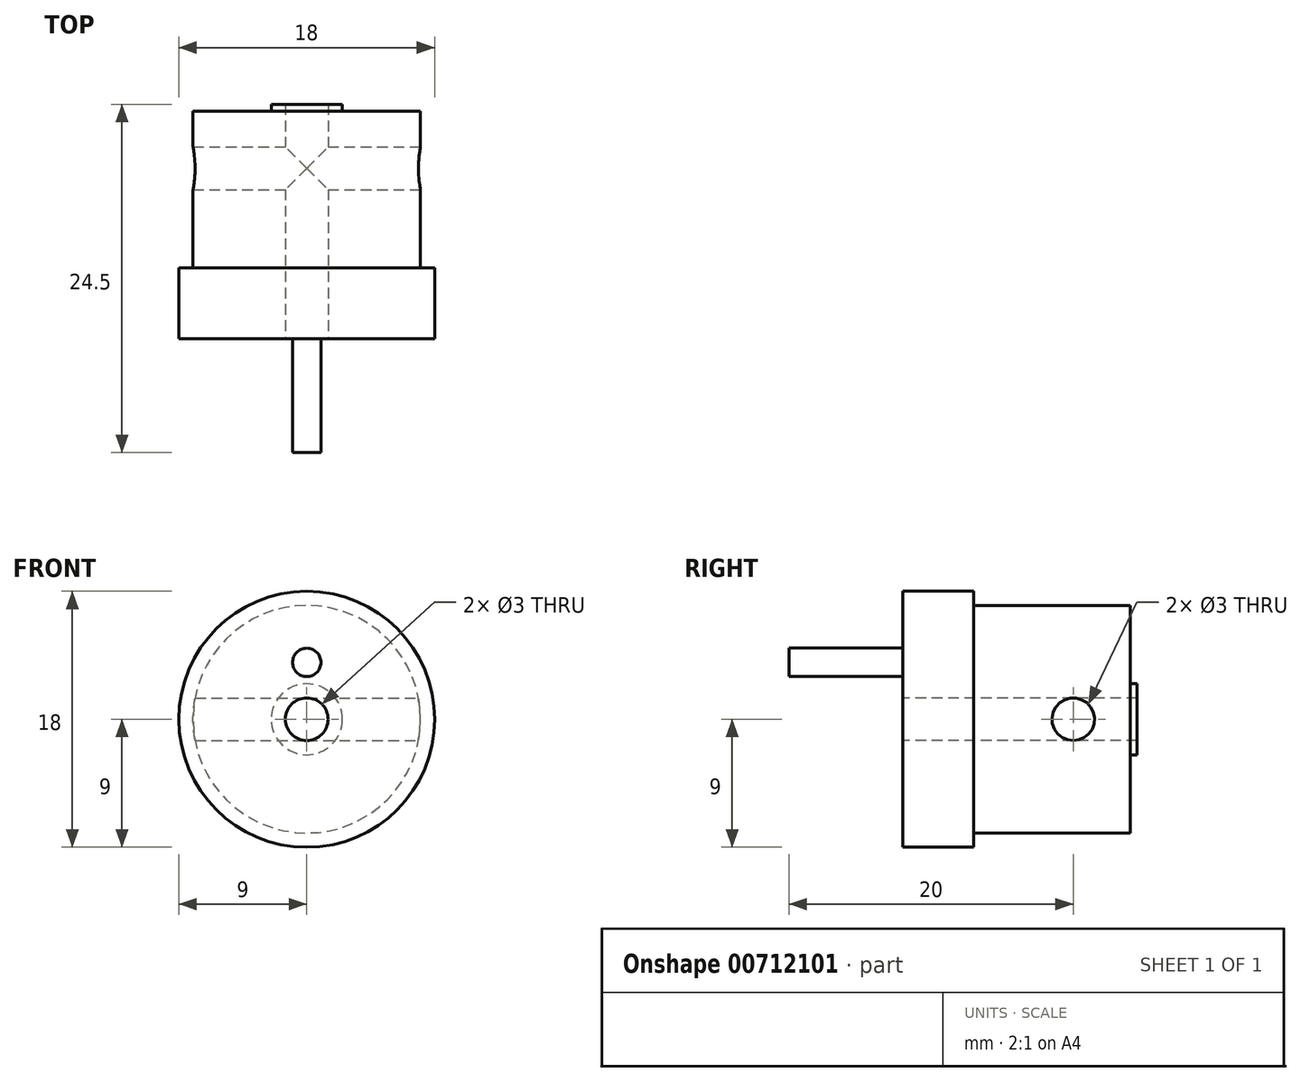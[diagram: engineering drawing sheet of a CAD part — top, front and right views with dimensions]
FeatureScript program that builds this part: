
annotation { "Feature Type Name" : "Feature", "Feature Type Description" : "" }
export const myFeature = defineFeature(function(context is Context, id is Id, definition is map)
    precondition{}
    {
        {
            var Q0;
            Q0=qCreatedBy(makeId("Front.planeOp"),FACE);
            var sketch = newSketch(context, id + "F0", { "sketchPlane" : qUnion([Q0])});
            skCircle(sketch, "E0", {"center": v(0, 0) * mm, "radius": 9 * mm});
            skCircle(sketch, "E1", {"center": v(0, 0) * mm, "radius": 8 * mm});
            skSolve(sketch);
        }
        {
            var Q0;
            Q0=makeQuery(id+"F0.imprint","IMPRINT",FACE,{"disambiguationData":[TD([[makeQuery(id+"F0.imprint","IMPRINT",EDGE,{"derivedFrom":sQuery(id+"F0.wireOp",EDGE,"E0")}),1.0]])]});
            var Q1;
            Q1=makeQuery(id+"F0.imprint","IMPRINT",FACE,{"disambiguationData":[TD([[makeQuery(id+"F0.imprint","IMPRINT",EDGE,{"derivedFrom":sQuery(id+"F0.wireOp",EDGE,"E1")}),1.0]])]});
            extrude(context, id + "F1", {"entities" : qUnion([Q0, Q1]), "depth" : 5 * mm, "offsetDistance" : 25 * mm});
        }
        {
            var Q0;
            Q0=makeQuery(id+"F0.imprint","IMPRINT",FACE,{"disambiguationData":[TD([[makeQuery(id+"F0.imprint","IMPRINT",EDGE,{"derivedFrom":sQuery(id+"F0.wireOp",EDGE,"E1")}),1.0]])]});
            extrude(context, id + "F2", {"entities" : qUnion([Q0]), "operationType" : NewBodyOperationType.ADD, "oppositeDirection" : true, "depth" : 11 * mm, "offsetDistance" : 25 * mm});
        }
        {
            var Q0;
            Q0=makeQuery(id+"F2.opExtrude","CAP_FACE",FACE,{"disambiguationData":[OSD([sQuery(id+"F0.wireOp",EDGE,"E1")])],"isStart":false});
            var sketch = newSketch(context, id + "F3", { "sketchPlane" : qUnion([Q0])});
            skCircle(sketch, "E2", {"center": v(0, 0) * mm, "radius": 2.5 * mm});
            skSolve(sketch);
        }
        {
            var Q0;
            Q0=makeQuery(id+"F3.imprint","IMPRINT",FACE,{"disambiguationData":[TD([[makeQuery(id+"F3.imprint","IMPRINT",EDGE,{"derivedFrom":sQuery(id+"F3.wireOp",EDGE,"E2")}),1.0]])]});
            extrude(context, id + "F4", {"entities" : qUnion([Q0]), "operationType" : NewBodyOperationType.ADD, "depth" : .5 * mm, "offsetDistance" : 25 * mm});
        }
        {
            var Q0;
            Q0=makeQuery(id+"F1.opExtrude","CAP_FACE",FACE,{"disambiguationData":[OSD([sQuery(id+"F0.wireOp",EDGE,"E0")])],"isStart":false});
            var sketch = newSketch(context, id + "F5", { "sketchPlane" : qUnion([Q0])});
            skCircle(sketch, "E3", {"center": v(0, 0) * mm, "radius": 1.5 * mm});
            skLineSegment(sketch, "E4", {"start": v(12.53, 0) * mm, "end": v(-19.66, 0) * mm, "construction": true});
            skLineSegment(sketch, "E5.0", {"start": v(12.53, 4) * mm, "end": v(-19.66, 4) * mm, "construction": true});
            skCircle(sketch, "E6", {"center": v(0, 4) * mm, "radius": 1 * mm});
            skSolve(sketch);
        }
        {
            var Q0;
            Q0=makeQuery(id+"F5.imprint","IMPRINT",FACE,{"disambiguationData":[TD([[makeQuery(id+"F5.imprint","IMPRINT",EDGE,{"derivedFrom":sQuery(id+"F5.wireOp",EDGE,"E3")}),1.0]])]});
            extrude(context, id + "F6", {"entities" : qUnion([Q0]), "operationType" : NewBodyOperationType.REMOVE, "oppositeDirection" : true, "depth" : 25 * mm, "offsetDistance" : 25 * mm});
        }
        {
            var Q0;
            Q0=makeQuery(id+"F5.imprint","IMPRINT",FACE,{"disambiguationData":[TD([[makeQuery(id+"F5.imprint","IMPRINT",EDGE,{"derivedFrom":sQuery(id+"F5.wireOp",EDGE,"E6")}),1.0]])]});
            extrude(context, id + "F7", {"entities" : qUnion([Q0]), "operationType" : NewBodyOperationType.ADD, "depth" : 8 * mm, "offsetDistance" : 25 * mm});
        }
        {
            var Q0;
            Q0=qCreatedBy(makeId("Right.planeOp"),FACE);
            var sketch = newSketch(context, id + "F8", { "sketchPlane" : qUnion([Q0])});
            skCircle(sketch, "E7", {"center": v(7, 0) * mm, "radius": 1.5 * mm});
            skSolve(sketch);
        }
        {
            var Q0;
            Q0=qSketchRegion(id+"F8",true);
            extrude(context, id + "F9", {"entities" : qUnion([Q0]), "operationType" : NewBodyOperationType.REMOVE, "endBound" : BoundingType.THROUGH_ALL, "oppositeDirection" : true, "depth" : 25 * mm, "offsetDistance" : 25 * mm, "hasSecondDirection" : true, "secondDirectionBound" : BoundingType.THROUGH_ALL, "secondDirectionOppositeDirection" : false, "secondDirectionDepth" : 25 * mm});
        }
    });
